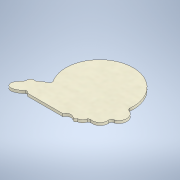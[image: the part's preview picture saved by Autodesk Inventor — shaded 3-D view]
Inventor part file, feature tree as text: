
AUTODESK INVENTOR PART (.ipt)
format: ipt  version: 2021 (Build 250183000, 183)  size: 138,240 bytes
history: native  units: mm
features: extrude x1, sketch x1
ambient origin geometry x8: Origin, YZ Plane, XZ Plane, XY Plane, X Axis, Y Axis, Z Axis, Center Point
bodies: Solid1 (feature_tree)
feature tree (2):
  extrude  "Extrusion1"  Depth=1.7mm TaperAngle=0.0deg
  sketch  "Sketch1"  dims[d5=42.5mm d36=1.7mm d37=0.0mm]
